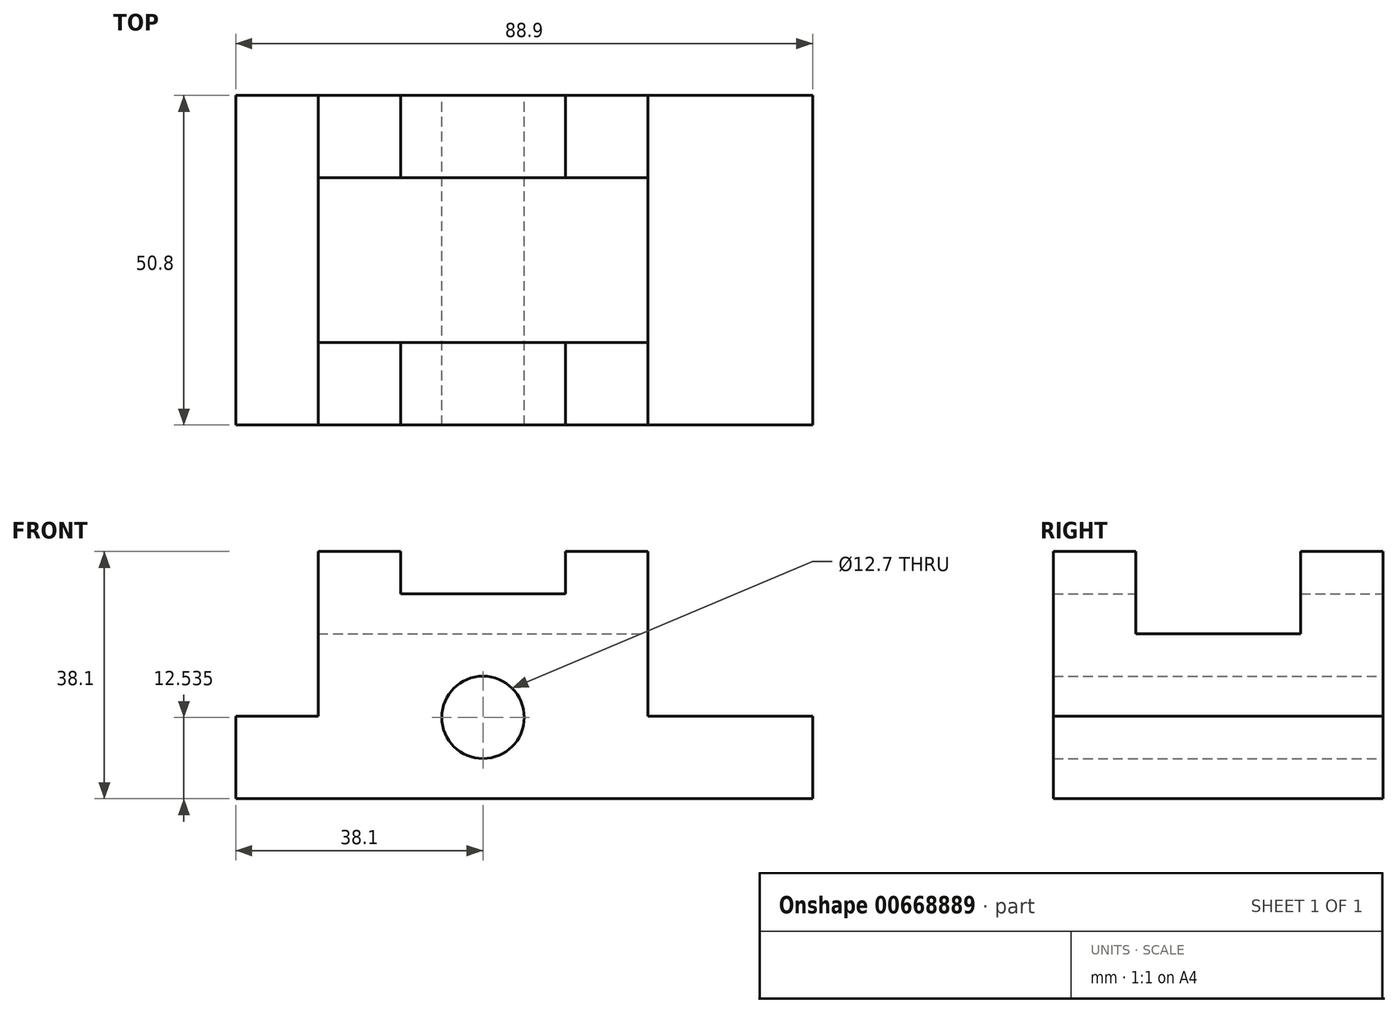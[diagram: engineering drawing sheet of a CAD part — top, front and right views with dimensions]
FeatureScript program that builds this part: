
annotation { "Feature Type Name" : "Feature", "Feature Type Description" : "" }
export const myFeature = defineFeature(function(context is Context, id is Id, definition is map)
    precondition{}
    {
        {
            var Q0;
            Q0=qCreatedBy(makeId("Front.planeOp"),FACE);
            var sketch = newSketch(context, id + "F0", { "sketchPlane" : qUnion([Q0])});
            skLineSegment(sketch, "E0", {"start": v(-88.9, -4.72) * mm, "end": v(-88.9, -17.42) * mm});
            skLineSegment(sketch, "E1", {"start": v(-88.9, -17.42) * mm, "end": v(0, -17.42) * mm});
            skLineSegment(sketch, "E2", {"start": v(0, -17.42) * mm, "end": v(0, -4.72) * mm});
            skLineSegment(sketch, "E3", {"start": v(0, -4.72) * mm, "end": v(-25.4, -4.72) * mm});
            skLineSegment(sketch, "E4", {"start": v(-25.4, -4.72) * mm, "end": v(-25.4, 20.68) * mm});
            skLineSegment(sketch, "E5", {"start": v(-25.4, 20.68) * mm, "end": v(-38.1, 20.68) * mm});
            skLineSegment(sketch, "E6", {"start": v(-38.1, 20.68) * mm, "end": v(-38.1, 14.17) * mm});
            skLineSegment(sketch, "E7", {"start": v(-38.1, 14.17) * mm, "end": v(-63.5, 14.17) * mm});
            skLineSegment(sketch, "E8", {"start": v(-63.5, 14.17) * mm, "end": v(-63.5, 20.68) * mm});
            skLineSegment(sketch, "E9", {"start": v(-63.5, 20.68) * mm, "end": v(-76.2, 20.68) * mm});
            skLineSegment(sketch, "E10", {"start": v(-76.2, 20.68) * mm, "end": v(-76.2, -4.72) * mm});
            skLineSegment(sketch, "E11", {"start": v(-76.2, -4.72) * mm, "end": v(-88.9, -4.72) * mm});
            skSolve(sketch);
        }
        {
            var Q0;
            Q0=makeQuery(id+"F0.imprint","IMPRINT",FACE,{"disambiguationData":[TD([[makeQuery(id+"F0.imprint","IMPRINT",EDGE,{"derivedFrom":sQuery(id+"F0.wireOp",EDGE,"E0")}),1.0]])]});
            extrude(context, id + "F1", {"entities" : qUnion([Q0]), "depth" : 50.8 * mm, "offsetDistance" : 25.4 * mm});
        }
        {
            var Q0;
            Q0=qCreatedBy(makeId("Front.planeOp"),FACE);
            var sketch = newSketch(context, id + "F2", { "sketchPlane" : qUnion([Q0])});
            skCircle(sketch, "E12", {"center": v(-50.8, -4.88) * mm, "radius": 6.35 * mm});
            skSolve(sketch);
        }
        {
            var Q0;
            Q0=makeQuery(id+"F2.imprint","IMPRINT",FACE,{"disambiguationData":[TD([[makeQuery(id+"F2.imprint","IMPRINT",EDGE,{"derivedFrom":sQuery(id+"F2.wireOp",EDGE,"E12")}),1.0]])]});
            var Q1;
            Q1=sQuery(id+"F2.wireOp",EDGE,"E12");
            extrude(context, id + "F3", {"entities" : qUnion([Q0]), "operationType" : NewBodyOperationType.REMOVE, "surfaceEntities" : qUnion([Q1]), "endBound" : BoundingType.THROUGH_ALL, "depth" : 50.8 * mm, "offsetDistance" : 25.4 * mm});
        }
        {
            var Q0;
            Q0=qCreatedBy(makeId("Right.planeOp"),FACE);
            var sketch = newSketch(context, id + "F4", { "sketchPlane" : qUnion([Q0])});
            skLineSegment(sketch, "E13.bottom", {"start": v(-38.1, 20.68) * mm, "end": v(-12.7, 20.68) * mm});
            skLineSegment(sketch, "E13.top", {"start": v(-38.1, 7.98) * mm, "end": v(-12.7, 7.98) * mm});
            skLineSegment(sketch, "E13.left", {"start": v(-38.1, 20.68) * mm, "end": v(-38.1, 7.98) * mm});
            skLineSegment(sketch, "E13.right", {"start": v(-12.7, 20.68) * mm, "end": v(-12.7, 7.98) * mm});
            skSolve(sketch);
        }
        {
            var Q0;
            Q0=makeQuery(id+"F4.imprint","IMPRINT",FACE,{"disambiguationData":[TD([[makeQuery(id+"F4.imprint","IMPRINT",EDGE,{"derivedFrom":sQuery(id+"F4.wireOp",EDGE,"E13.bottom")}),-1.0]])]});
            extrude(context, id + "F5", {"entities" : qUnion([Q0]), "operationType" : NewBodyOperationType.REMOVE, "endBound" : BoundingType.THROUGH_ALL, "oppositeDirection" : true, "depth" : 88.9 * mm, "offsetDistance" : 25.4 * mm});
        }
    });
